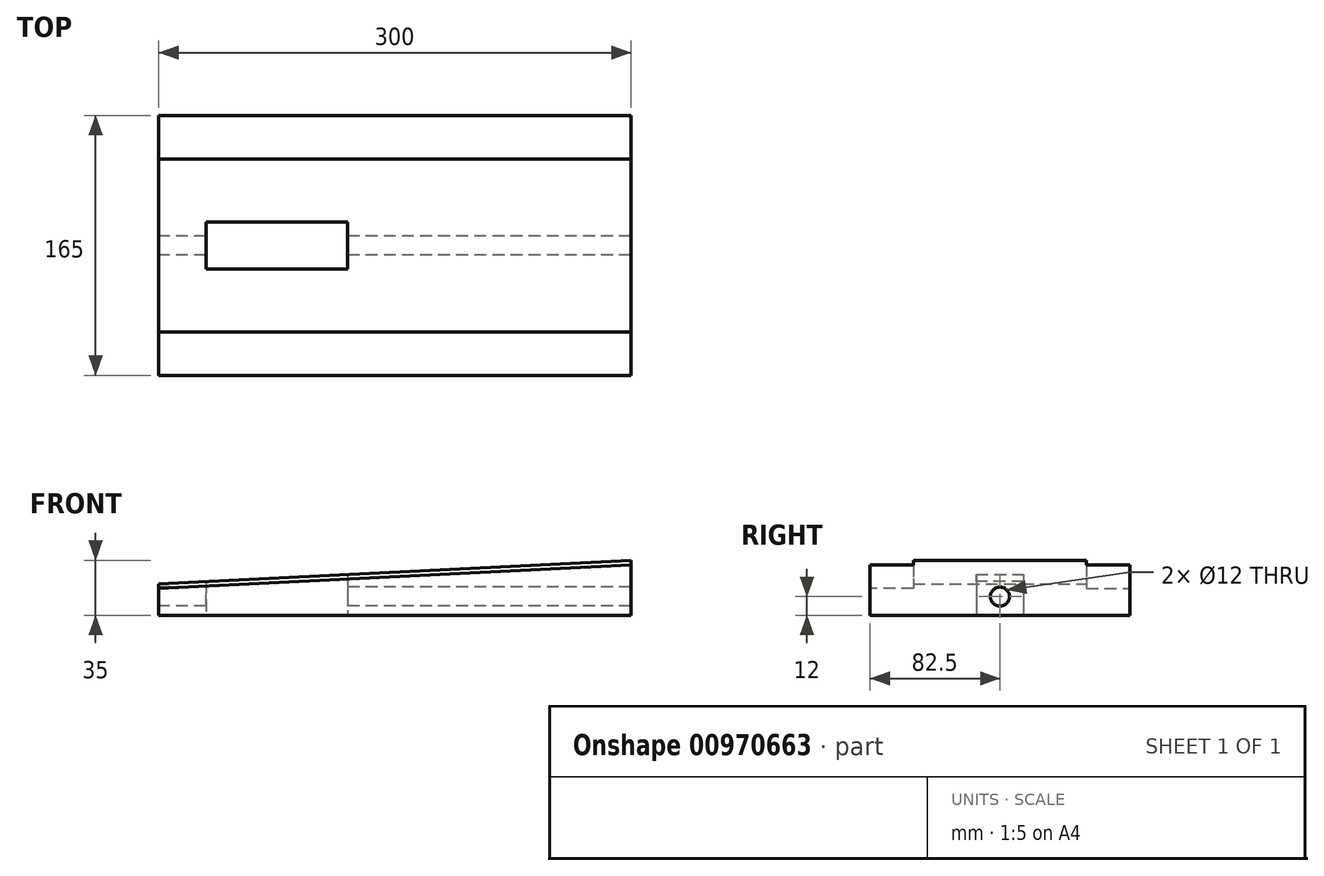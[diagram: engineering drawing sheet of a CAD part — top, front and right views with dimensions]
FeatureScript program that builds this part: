
annotation { "Feature Type Name" : "Feature", "Feature Type Description" : "" }
export const myFeature = defineFeature(function(context is Context, id is Id, definition is map)
    precondition{}
    {
        {
            var Q0;
            Q0=qCreatedBy(makeId("Front.planeOp"),FACE);
            var sketch = newSketch(context, id + "F0", { "sketchPlane" : qUnion([Q0])});
            skLineSegment(sketch, "E0", {"start": v(0, 0) * mm, "end": v(300, 0) * mm});
            skLineSegment(sketch, "E1", {"start": v(300, 0) * mm, "end": v(300, 35) * mm});
            skLineSegment(sketch, "E2", {"start": v(300, 35) * mm, "end": v(0, 20) * mm});
            skLineSegment(sketch, "E3", {"start": v(0, 20) * mm, "end": v(0, 0) * mm});
            skSolve(sketch);
        }
        {
            var Q0;
            Q0=makeQuery(id+"F0.imprint","IMPRINT",FACE,{"disambiguationData":[TD([[makeQuery(id+"F0.imprint","IMPRINT",EDGE,{"derivedFrom":sQuery(id+"F0.wireOp",EDGE,"E0")}),1.0]])]});
            extrude(context, id + "F1", {"entities" : qUnion([Q0]), "depth" : 165 * mm, "offsetDistance" : 25 * mm});
        }
        {
            var Q0;
            Q0=makeQuery(id+"F1.opExtrude","SWEPT_FACE",FACE,{"disambiguationData":[OSD([sQuery(id+"F0.wireOp",EDGE,"E0")])]});
            var sketch = newSketch(context, id + "F2", { "sketchPlane" : qUnion([Q0])});
            skLineSegment(sketch, "E4", {"start": v(30, 97.5) * mm, "end": v(120, 97.5) * mm});
            skLineSegment(sketch, "E5", {"start": v(120, 97.5) * mm, "end": v(120, 67.5) * mm});
            skLineSegment(sketch, "E6", {"start": v(120, 67.5) * mm, "end": v(30, 67.5) * mm});
            skLineSegment(sketch, "E7", {"start": v(30, 67.5) * mm, "end": v(30, 97.5) * mm});
            skSolve(sketch);
        }
        {
            var Q0;
            Q0=makeQuery(id+"F2.imprint","IMPRINT",FACE,{"disambiguationData":[TD([[makeQuery(id+"F2.imprint","IMPRINT",EDGE,{"derivedFrom":sQuery(id+"F2.wireOp",EDGE,"E4")}),-1.0]])]});
            extrude(context, id + "F3", {"entities" : qUnion([Q0]), "operationType" : NewBodyOperationType.REMOVE, "endBound" : BoundingType.THROUGH_ALL, "oppositeDirection" : true, "depth" : 25 * mm, "offsetDistance" : 25 * mm});
        }
        {
            var Q0;
            Q0=makeQuery(id+"F1.opExtrude","SWEPT_FACE",FACE,{"disambiguationData":[OSD([sQuery(id+"F0.wireOp",EDGE,"E3")])]});
            var sketch = newSketch(context, id + "F4", { "sketchPlane" : qUnion([Q0])});
            skCircle(sketch, "E8", {"center": v(82.5, 12) * mm, "radius": 6 * mm});
            skSolve(sketch);
        }
        {
            var Q0;
            Q0=makeQuery(id+"F4.imprint","IMPRINT",FACE,{"disambiguationData":[TD([[makeQuery(id+"F4.imprint","IMPRINT",EDGE,{"derivedFrom":sQuery(id+"F4.wireOp",EDGE,"E8")}),1.0]])]});
            extrude(context, id + "F5", {"entities" : qUnion([Q0]), "operationType" : NewBodyOperationType.REMOVE, "flatOperationType" : FlatOperationType.REMOVE, "endBound" : BoundingType.THROUGH_ALL, "oppositeDirection" : true, "depth" : 80 * mm, "offsetDistance" : 25 * mm, "domain" : OperationDomain.MODEL});
        }
        {
            var Q0;
            Q0=qCreatedBy(makeId("Front.planeOp"),FACE);
            var sketch = newSketch(context, id + "F6", { "sketchPlane" : qUnion([Q0])});
            skLineSegment(sketch, "E9.0", {"start": v(399.4, 36.97) * mm, "end": v(-0.13, 16.99) * mm});
            skLineSegment(sketch, "E10.0", {"start": v(399.4, 39.97) * mm, "end": v(-0.13, 20) * mm});
            skLineSegment(sketch, "E11", {"start": v(-0.13, 20) * mm, "end": v(-0.13, 16.99) * mm});
            skLineSegment(sketch, "E12", {"start": v(399.4, 39.97) * mm, "end": v(399.4, 36.97) * mm});
            skSolve(sketch);
        }
        {
            var Q0;
            Q0 = qSketchRegion(id + "F6", true);
            extrude(context, id + "F7", {"entities" : qUnion([Q0]), "operationType" : NewBodyOperationType.REMOVE, "depth" : 27.5 * mm, "offsetDistance" : 25 * mm});
        }
        {
            var Q0;
            Q0=makeQuery(id+"F1.opExtrude","CAP_FACE",FACE,{"disambiguationData":[OSD([sQuery(id+"F0.wireOp",EDGE,"E0"),sQuery(id+"F0.wireOp",EDGE,"E1"),sQuery(id+"F0.wireOp",EDGE,"E2"),sQuery(id+"F0.wireOp",EDGE,"E3")])],"isStart":false});
            var sketch = newSketch(context, id + "F8", { "sketchPlane" : qUnion([Q0])});
            skLineSegment(sketch, "E13.0", {"start": v(300, 32) * mm, "end": v(0, 17) * mm});
            skLineSegment(sketch, "E14", {"start": v(0, 20) * mm, "end": v(0, 17) * mm});
            skLineSegment(sketch, "E15", {"start": v(300, 35) * mm, "end": v(300, 32) * mm});
            skLineSegment(sketch, "E16", {"start": v(0, 20) * mm, "end": v(300, 35) * mm});
            skSolve(sketch);
        }
        {
            var Q0;
            Q0 = qSketchRegion(id + "F8", true);
            extrude(context, id + "F9", {"entities" : qUnion([Q0]), "operationType" : NewBodyOperationType.REMOVE, "oppositeDirection" : true, "depth" : 27.5 * mm, "offsetDistance" : 25 * mm});
        }
    });
